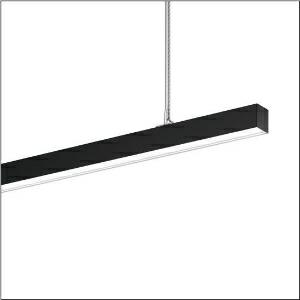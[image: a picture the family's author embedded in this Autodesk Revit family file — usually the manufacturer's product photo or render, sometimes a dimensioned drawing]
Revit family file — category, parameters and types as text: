
# Revit family: silica_r__21_51mx30tbt5b_11dd
name_source: partatom
category: Lighting Fixtures
units: mm (PartAtom-declared; Revit-internal decimal feet)

## family parameters
Cut with Voids When Loaded = No
Host = Face
Light Source = No
Part Type = Normal
Room Calculation Point = No
Round Connector Dimension = Use Diameter
Shared = No

## types (1)
- --- (1 x LED, 5150 lm, 42.2 W, 6500K)
    Apparent Load = 42 VA
    CIE Flux Codes = 47 79 96 58 100
    Color Rendering = 80
    Color Temperature = 6500K
    Default Elevation = 1800 mm
    Description = Silica® 21, office luminaire, primary optical cover: cover, of PMMA, opal, light emission: direct/indirect distribution, primary light characteristic: symmetric, installation type: suspended mounting, LED, rated luminous flux: 5.150lm, luminous efficacy: 116lm/W, light colour: 8tw, colour temperature: 2700..6500K, control gear: ECG DALI, with terminal, 3+2-pole, max. 2.5mm², mains connection: 220..240V, AC, 50/60Hz, rated input power: 44.3W, luminaire housing, of aluminium, jet black (RAL 9005), length: 1.504mm, width: 53mm, height: 53mm, protection rating (complete): IP20, insulation class (complete): insulation class I (protective earthing), certification: CE, permissible operating ambient temperature: 0..+35°C, standard: EN 50419, packaging unit: 1 piece
    Height = 53 mm
    Lamp = 1 x LED
    Lamp Light Flux = 5150 lm
    Lamp Power = 42.2 W
    Lamp count = 1
    Length = 1504 mm
    Luminous efficacy = 122 lm/W
    Manufacturer = Siteco
    ModVariant = No
    Model = 51MX30TBT5B
    Mounting Place = Ceiling
    Mounting Type = Pendant
    Number of Poles = 1
    OnlyDefault = Yes
    Power Factor = 1
    Product Name = Silica® 21
    Product group = office luminaire | ceiling pendant
    ProductGroupID = 905
    Protection Class = Protection class I
    Protection Degree = IP 20
    RLX_Detail_Level = 1
    RlxData = <blob elided: 22869 chars, md5=9d1f9abe>
    Socket = socket
    Standby Power = 0 W
    System Light Flux = 5150 lm
    System Power = 42 W
    Type Comments = individual setting
    Type Image = l_1251735.jpg
    URL = http://relux.com
    VarID = @adj_045723
    Voltage = 0 V
    Weight = 0.00 kg
    Width = 53 mm

## geometry (parser evidence)
native form markers: Blend x4, Sweep x12
no freeform markers — native parametric forms only
